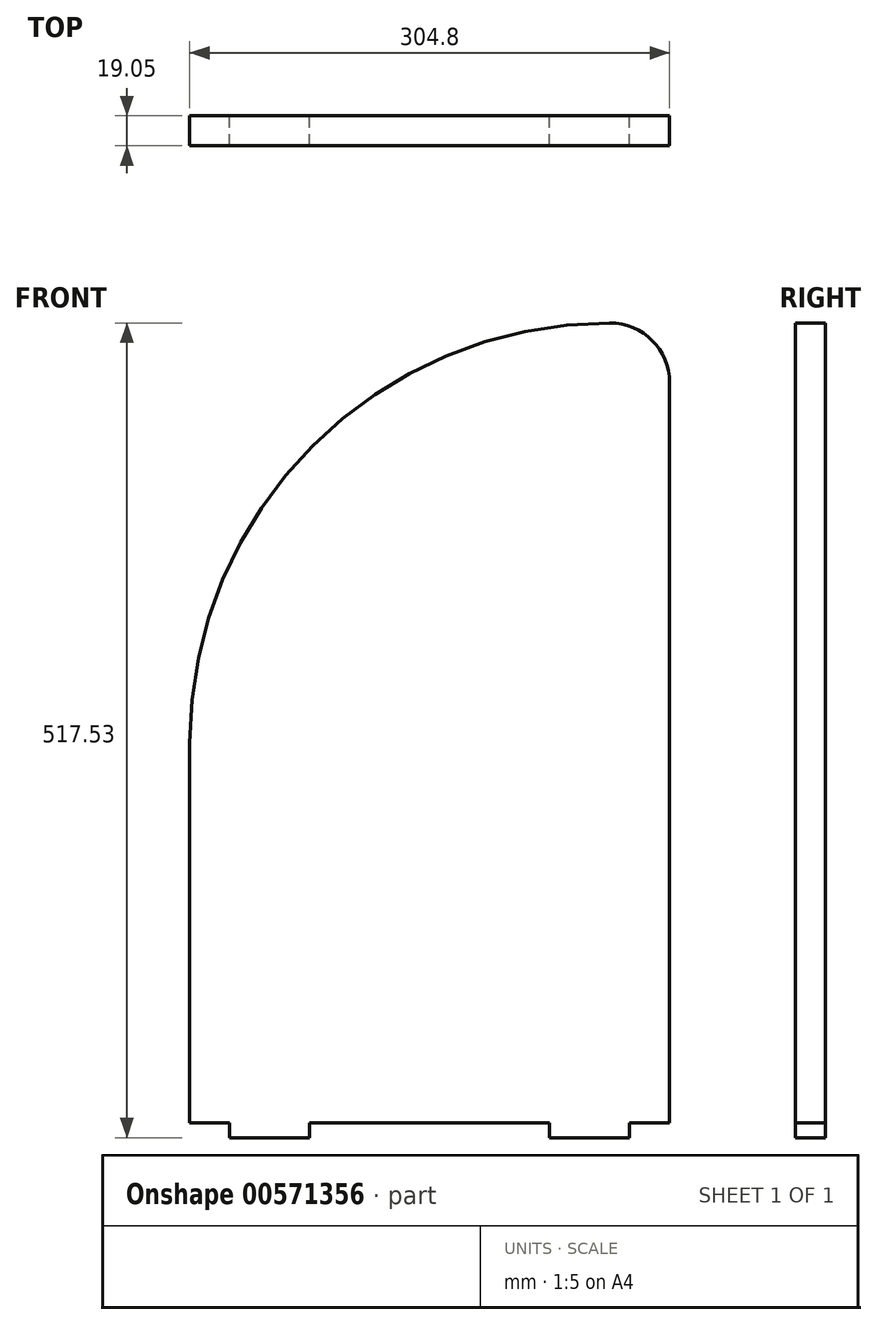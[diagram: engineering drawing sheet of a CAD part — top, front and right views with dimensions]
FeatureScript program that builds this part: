
annotation { "Feature Type Name" : "Feature", "Feature Type Description" : "" }
export const myFeature = defineFeature(function(context is Context, id is Id, definition is map)
    precondition{}
    {
        {
            var Q0;
            Q0=qCreatedBy(makeId("Front.planeOp"),FACE);
            var sketch = newSketch(context, id + "F0", { "sketchPlane" : qUnion([Q0])});
            skLineSegment(sketch, "E0", {"start": v(-142.72, -132.92) * mm, "end": v(-117.32, -132.92) * mm});
            skLineSegment(sketch, "E1", {"start": v(-142.72, -132.92) * mm, "end": v(-142.72, 108.38) * mm});
            skLineSegment(sketch, "E2", {"start": v(123.98, 375.08) * mm, "end": v(123.98, 375.08) * mm});
            skLineSegment(sketch, "E3", {"start": v(162.08, 336.98) * mm, "end": v(162.08, -132.92) * mm});
            skPoint(sketch, "E4.visualSharp", {"position": v(-142.72, 375.08) * mm});
            skArc(sketch, "E4.filletArc", {"start": v(123.98, 375.08) * mm, "mid": v(-64.6, 296.96) * mm, "end": v(-142.72, 108.38) * mm});
            skLineSegment(sketch, "E5", {"start": v(-117.32, -132.92) * mm, "end": v(-117.32, -142.45) * mm});
            skLineSegment(sketch, "E6", {"start": v(-117.32, -142.45) * mm, "end": v(-66.52, -142.45) * mm});
            skLineSegment(sketch, "E7", {"start": v(-66.52, -142.45) * mm, "end": v(-66.52, -132.92) * mm});
            skLineSegment(sketch, "E8.trimOffspring", {"start": v(-66.52, -132.92) * mm, "end": v(85.88, -132.92) * mm});
            skLineSegment(sketch, "E9", {"start": v(85.88, -132.92) * mm, "end": v(85.88, -142.45) * mm});
            skLineSegment(sketch, "E10", {"start": v(85.88, -142.45) * mm, "end": v(136.68, -142.45) * mm});
            skLineSegment(sketch, "E11", {"start": v(136.68, -142.45) * mm, "end": v(136.68, -132.92) * mm});
            skLineSegment(sketch, "E12.trimOffspring", {"start": v(136.68, -132.92) * mm, "end": v(162.08, -132.92) * mm});
            skPoint(sketch, "E13.visualSharp", {"position": v(162.08, 375.08) * mm});
            skArc(sketch, "E13.filletArc", {"start": v(162.08, 336.98) * mm, "mid": v(150.92, 363.92) * mm, "end": v(123.98, 375.08) * mm});
            skSolve(sketch);
        }
        {
            var Q0;
            Q0=makeQuery(id+"F0.imprint","IMPRINT",FACE,{"disambiguationData":[TD([[makeQuery(id+"F0.imprint","IMPRINT",EDGE,{"derivedFrom":sQuery(id+"F0.wireOp",EDGE,"E0")}),1.0]])]});
            extrude(context, id + "F1", {"entities" : qUnion([Q0]), "depth" : 19.05 * mm, "offsetDistance" : 25.4 * mm});
        }
    });
